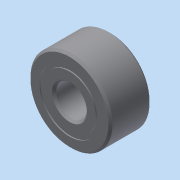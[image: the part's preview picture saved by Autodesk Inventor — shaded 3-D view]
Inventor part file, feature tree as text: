
AUTODESK INVENTOR PART (.ipt)
format: ipt  version: 2015 (Build 190159000, 159)  size: 605,184 bytes
history: native  units: in
note: dims shown in document units (in); Inventor stores cm internally (conversion verified against a paired STEP export)
features: imported_body x16, other x12, revolve x5
ambient origin geometry x8: Origin, YZ Plane, XZ Plane, XY Plane, X Axis, Y Axis, Z Axis, Center Point
bodies: Body1 (feature_tree), Body2 (feature_tree), Body3 (feature_tree), Body4 (feature_tree), Body5 (feature_tree), Body6 (feature_tree), Body7 (feature_tree), Body8 (feature_tree), Body9 (feature_tree), Body10 (feature_tree), Body11 (feature_tree), Body12 (feature_tree), Body13 (feature_tree), Body14 (feature_tree), Body15 (feature_tree), Body16 (feature_tree)
feature tree (33):
  revolve  "Revolve1"  [1 undecoded]
  other  "7804K1261"
  revolve  "Revolve3"  [1 undecoded]
  revolve  "Revolve4"  [1 undecoded]
  other  "CirPattern1[1]"
  other  "CirPattern1[2]"
  other  "CirPattern1[3]"
  other  "CirPattern1[4]"
  other  "CirPattern1[5]"
  other  "CirPattern1[6]"
  other  "CirPattern1[7]"
  other  "CirPattern1[8]"
  other  "CirPattern1[9]"
  other  "CirPattern1[10]"
  other  "CirPattern1[11]"
  revolve  "Revolve5[1]"  [1 undecoded]
  revolve  "Revolve5[2]"  [1 undecoded]
  imported_body  "Base1"
  imported_body  "Base2"
  imported_body  "Base3"
  imported_body  "Base4"
  imported_body  "Base5"
  imported_body  "Base6"
  imported_body  "Base7"
  imported_body  "Base8"
  imported_body  "Base9"
  imported_body  "Base10"
  imported_body  "Base11"
  imported_body  "Base12"
  imported_body  "Base13"
  imported_body  "Base14"
  imported_body  "Base15"
  imported_body  "Base16"
note: 5 required parameter values undecoded (feature->parameter linkage not recoverable at this tier; creation-order binding heuristic only, values carry confidence <= 0.55)
